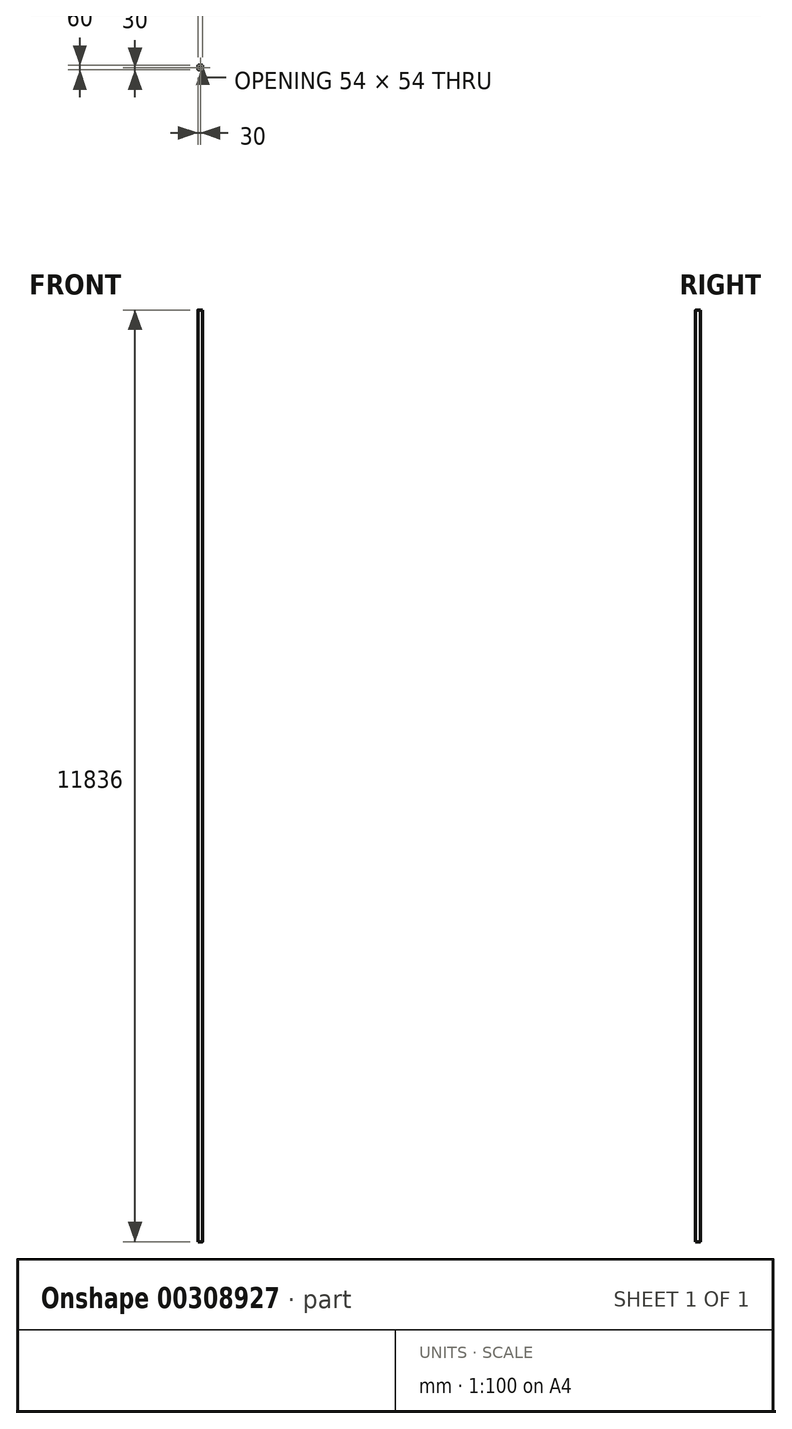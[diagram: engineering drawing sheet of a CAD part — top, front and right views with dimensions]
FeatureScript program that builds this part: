
annotation { "Feature Type Name" : "Feature", "Feature Type Description" : "" }
export const myFeature = defineFeature(function(context is Context, id is Id, definition is map)
    precondition{}
    {
        {
            var Q0;
            Q0=qCreatedBy(makeId("Top.planeOp"),FACE);
            var sketch = newSketch(context, id + "F0", { "sketchPlane" : qUnion([Q0])});
            skLineSegment(sketch, "E0.bottom", {"start": v(24, 30) * mm, "end": v(-24, 30) * mm});
            skLineSegment(sketch, "E0.top", {"start": v(24, -30) * mm, "end": v(-24, -30) * mm});
            skLineSegment(sketch, "E0.left", {"start": v(30, 24) * mm, "end": v(30, -24) * mm});
            skLineSegment(sketch, "E0.right", {"start": v(-30, 24) * mm, "end": v(-30, -24) * mm});
            skPoint(sketch, "E0.middle", {"position": v(0, 0) * mm});
            skLineSegment(sketch, "E1.0", {"start": v(27, 21) * mm, "end": v(27, -21) * mm});
            skLineSegment(sketch, "E1.1", {"start": v(21, 27) * mm, "end": v(-21, 27) * mm});
            skLineSegment(sketch, "E1.2", {"start": v(-27, 21) * mm, "end": v(-27, -21) * mm});
            skLineSegment(sketch, "E1.3", {"start": v(21, -27) * mm, "end": v(-21, -27) * mm});
            skPoint(sketch, "E2.visualSharp", {"position": v(-27, 27) * mm});
            skArc(sketch, "E2.filletArc", {"start": v(-21, 27) * mm, "mid": v(-25.24, 25.24) * mm, "end": v(-27, 21) * mm});
            skPoint(sketch, "E3.visualSharp", {"position": v(-27, -27) * mm});
            skArc(sketch, "E3.filletArc", {"start": v(-27, -21) * mm, "mid": v(-25.24, -25.24) * mm, "end": v(-21, -27) * mm});
            skPoint(sketch, "E4.visualSharp", {"position": v(27, -27) * mm});
            skArc(sketch, "E4.filletArc", {"start": v(21, -27) * mm, "mid": v(25.24, -25.24) * mm, "end": v(27, -21) * mm});
            skPoint(sketch, "E5.visualSharp", {"position": v(27, 27) * mm});
            skArc(sketch, "E5.filletArc", {"start": v(27, 21) * mm, "mid": v(25.24, 25.24) * mm, "end": v(21, 27) * mm});
            skPoint(sketch, "E6.visualSharp", {"position": v(30, 30) * mm});
            skArc(sketch, "E6.filletArc", {"start": v(30, 24) * mm, "mid": v(28.24, 28.24) * mm, "end": v(24, 30) * mm});
            skPoint(sketch, "E7.visualSharp", {"position": v(30, -30) * mm});
            skArc(sketch, "E7.filletArc", {"start": v(24, -30) * mm, "mid": v(28.24, -28.24) * mm, "end": v(30, -24) * mm});
            skPoint(sketch, "E8.visualSharp", {"position": v(-30, -30) * mm});
            skArc(sketch, "E8.filletArc", {"start": v(-30, -24) * mm, "mid": v(-28.24, -28.24) * mm, "end": v(-24, -30) * mm});
            skPoint(sketch, "E9.visualSharp", {"position": v(-30, 30) * mm});
            skArc(sketch, "E9.filletArc", {"start": v(-24, 30) * mm, "mid": v(-28.24, 28.24) * mm, "end": v(-30, 24) * mm});
            skSolve(sketch);
        }
        {
            var Q0;
            Q0 = qSketchRegion(id + "F0", true);
            extrude(context, id + "F1", {"entities" : qUnion([Q0]), "depth" : 11836 * mm});
        }
    });
